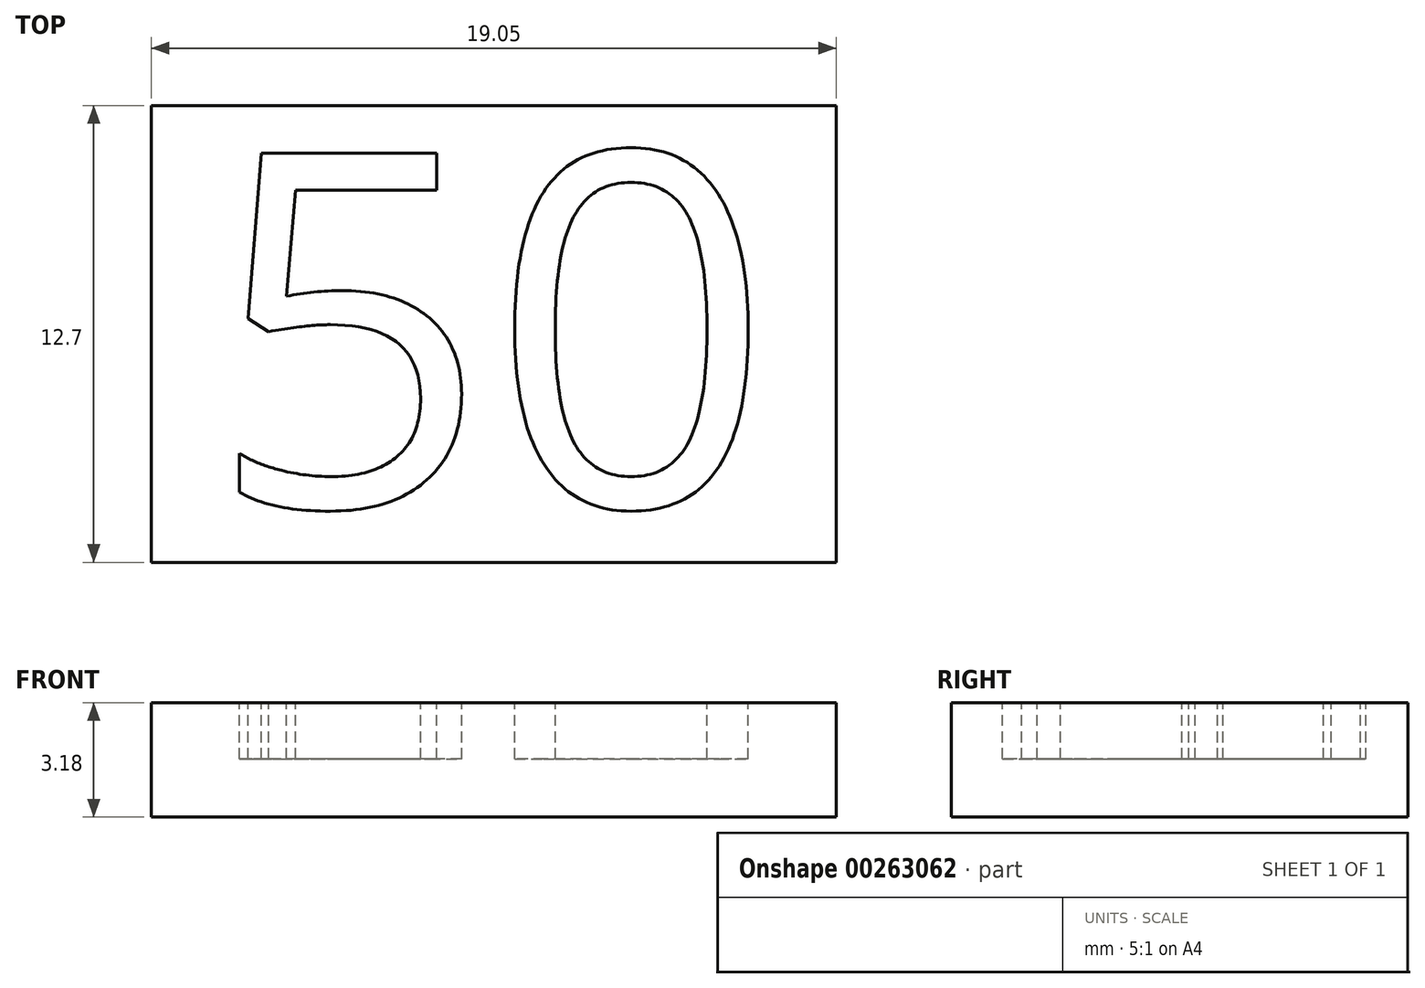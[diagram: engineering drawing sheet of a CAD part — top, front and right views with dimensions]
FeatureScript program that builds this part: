
annotation { "Feature Type Name" : "Feature", "Feature Type Description" : "" }
export const myFeature = defineFeature(function(context is Context, id is Id, definition is map)
    precondition{}
    {
        {
            var Q0;
            Q0=qCreatedBy(makeId("Top.planeOp"),FACE);
            var sketch = newSketch(context, id + "F0", { "sketchPlane" : qUnion([Q0])});
            skLineSegment(sketch, "E0.bottom", {"start": v(0, 0) * mm, "end": v(19.05, 0) * mm});
            skLineSegment(sketch, "E0.top", {"start": v(0, 12.7) * mm, "end": v(19.05, 12.7) * mm});
            skLineSegment(sketch, "E0.left", {"start": v(0, 0) * mm, "end": v(0, 12.7) * mm});
            skLineSegment(sketch, "E0.right", {"start": v(19.05, 0) * mm, "end": v(19.05, 12.7) * mm});
            skSolve(sketch);
        }
        {
            var Q0;
            Q0=makeQuery(id+"F0.imprint","IMPRINT",FACE,{"disambiguationData":[TD([[makeQuery(id+"F0.imprint","IMPRINT",EDGE,{"derivedFrom":sQuery(id+"F0.wireOp",EDGE,"E0.bottom")}),1.0]])]});
            extrude(context, id + "F1", {"entities" : qUnion([Q0]), "depth" : 3.17 * mm});
        }
        {
            var Q0;
            Q0=makeQuery(id+"F1.opExtrude","CAP_FACE",FACE,{"disambiguationData":[OSD([sQuery(id+"F0.wireOp",EDGE,"E0.bottom"),sQuery(id+"F0.wireOp",EDGE,"E0.top"),sQuery(id+"F0.wireOp",EDGE,"E0.left"),sQuery(id+"F0.wireOp",EDGE,"E0.right")])],"isStart":false});
            var sketch = newSketch(context, id + "F2", { "sketchPlane" : qUnion([Q0])});
            skLineSegment(sketch, "E1.0", {"start": v(0, 0) * mm, "end": v(19.05, 0) * mm});
            skLineSegment(sketch, "E2.0", {"start": v(0, 0) * mm, "end": v(0, 12.7) * mm});
            skLineSegment(sketch, "E3.0", {"start": v(0, 12.7) * mm, "end": v(19.05, 12.7) * mm});
            skLineSegment(sketch, "E4.0", {"start": v(19.05, 0) * mm, "end": v(19.05, 12.7) * mm});
            skText(sketch, "E5", { "text": "50", "fontName": "OpenSans-Regular.ttf"});
            const initialGuessF2  = {"E5": [0.00156, 0.00156, 1, 0, 0.0099]};
            skSetInitialGuess(sketch, initialGuessF2);
            skSolve(sketch);
        }
        {
            var Q0;
            Q0=makeQuery(id+"F2.imprint","IMPRINT",FACE,{"disambiguationData":[TD([[makeQuery(id+"F2.imprint","IMPRINT",EDGE,{"derivedFrom":sQuery(id+"F2.wireOp",EDGE,"E5.sketch_text.stroke-0")}),-1.0]])]});
            var Q1;
            Q1=makeQuery(id+"F2.imprint","IMPRINT",FACE,{"disambiguationData":[TD([[makeQuery(id+"F2.imprint","IMPRINT",EDGE,{"derivedFrom":sQuery(id+"F2.wireOp",EDGE,"E5.sketch_text.stroke-19")}),-1.0]])]});
            extrude(context, id + "F3", {"entities" : qUnion([Q0, Q1]), "operationType" : NewBodyOperationType.REMOVE, "oppositeDirection" : true, "depth" : 1.56 * mm});
        }
    });
